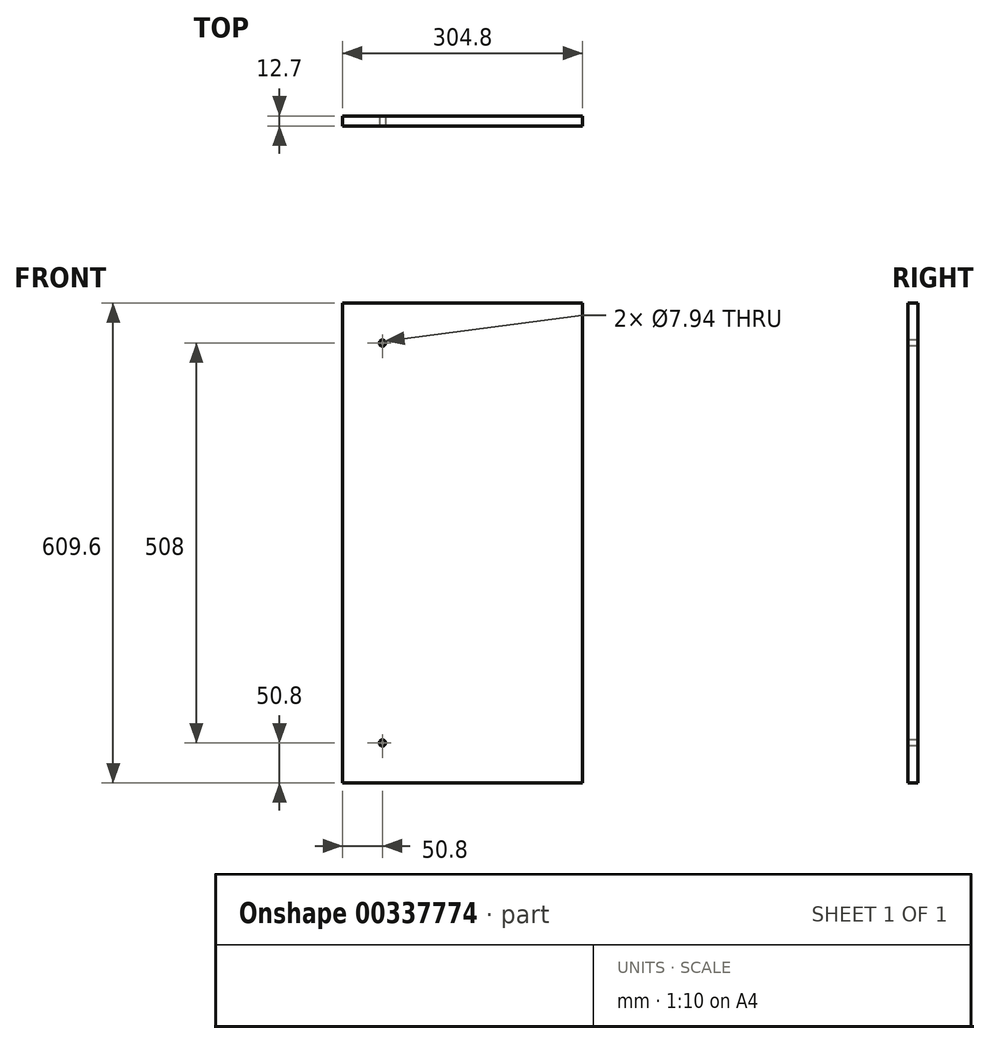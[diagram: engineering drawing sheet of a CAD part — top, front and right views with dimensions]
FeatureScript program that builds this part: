
annotation { "Feature Type Name" : "Feature", "Feature Type Description" : "" }
export const myFeature = defineFeature(function(context is Context, id is Id, definition is map)
    precondition{}
    {
        {
            var Q0;
            Q0=qCreatedBy(makeId("Front.planeOp"),FACE);
            var sketch = newSketch(context, id + "F0", { "sketchPlane" : qUnion([Q0])});
            skLineSegment(sketch, "E0.bottom", {"start": v(0, 0) * mm, "end": v(304.8, 0) * mm});
            skLineSegment(sketch, "E0.top", {"start": v(0, 609.6) * mm, "end": v(304.8, 609.6) * mm});
            skLineSegment(sketch, "E0.left", {"start": v(0, 0) * mm, "end": v(0, 609.6) * mm});
            skLineSegment(sketch, "E0.right", {"start": v(304.8, 0) * mm, "end": v(304.8, 609.6) * mm});
            skSolve(sketch);
        }
        {
            var Q0;
            Q0=makeQuery(id+"F0.imprint","IMPRINT",FACE,{"disambiguationData":[TD([[makeQuery(id+"F0.imprint","IMPRINT",EDGE,{"derivedFrom":sQuery(id+"F0.wireOp",EDGE,"E0.bottom")}),1.0]])]});
            extrude(context, id + "F1", {"entities" : qUnion([Q0]), "oppositeDirection" : true, "depth" : 12.7 * mm});
        }
        {
            var Q0;
            Q0=makeQuery(id+"F1.opExtrude","CAP_FACE",FACE,{"disambiguationData":[OSD([sQuery(id+"F0.wireOp",EDGE,"E0.bottom"),sQuery(id+"F0.wireOp",EDGE,"E0.top"),sQuery(id+"F0.wireOp",EDGE,"E0.left"),sQuery(id+"F0.wireOp",EDGE,"E0.right")])],"isStart":true});
            var sketch = newSketch(context, id + "F2", { "sketchPlane" : qUnion([Q0])});
            skLineSegment(sketch, "E1.bottom", {"start": v(50.8, 558.8) * mm, "end": v(254, 558.8) * mm});
            skLineSegment(sketch, "E1.top", {"start": v(50.8, 50.8) * mm, "end": v(254, 50.8) * mm});
            skLineSegment(sketch, "E1.left", {"start": v(50.8, 558.8) * mm, "end": v(50.8, 50.8) * mm});
            skLineSegment(sketch, "E1.right", {"start": v(254, 558.8) * mm, "end": v(254, 50.8) * mm});
            skSolve(sketch);
        }
        {
            var Q0;
            Q0=sQuery(id+"F2.wireOp",VERTEX,"E1.left.end");
            var Q1;
            Q1=sQuery(id+"F2.wireOp",VERTEX,"E1.bottom.start");
            var Q2;
            Q2=makeQuery(id+"F1.opExtrude","SWEPT_BODY",BODY,{"disambiguationData":[OSD([sQuery(id+"F0.wireOp",EDGE,"E0.bottom"),sQuery(id+"F0.wireOp",EDGE,"E0.top"),sQuery(id+"F0.wireOp",EDGE,"E0.left"),sQuery(id+"F0.wireOp",EDGE,"E0.right")])]});
            hole(context, id + "F3", {"style" : HoleStyle.SIMPLE, "endStyle" : HoleEndStyle.THROUGH, "standardTappedOrClearance" : lookupTablePath({ "standard" : "ANSI", "engagement" : "75%", "pitch" : "16 tpi", "size" : "3/8", "type" : "Tapped" }), "standardBlindInLast" : lookupTablePath({ "standard" : "ANSI", "engagement" : "75%", "pitch" : "16 tpi", "size" : "3/8", "type" : "Tapped" }), "holeDiameter" : 7.94 * mm, "showTappedDepth" : true, "tappedDepth" : 12.7 * mm, "tapClearance" : 3, "locations" : qUnion([Q0, Q1]), "scope" : qUnion([Q2]), "majorDiameter" : 9.53 * mm});
        }
    });
